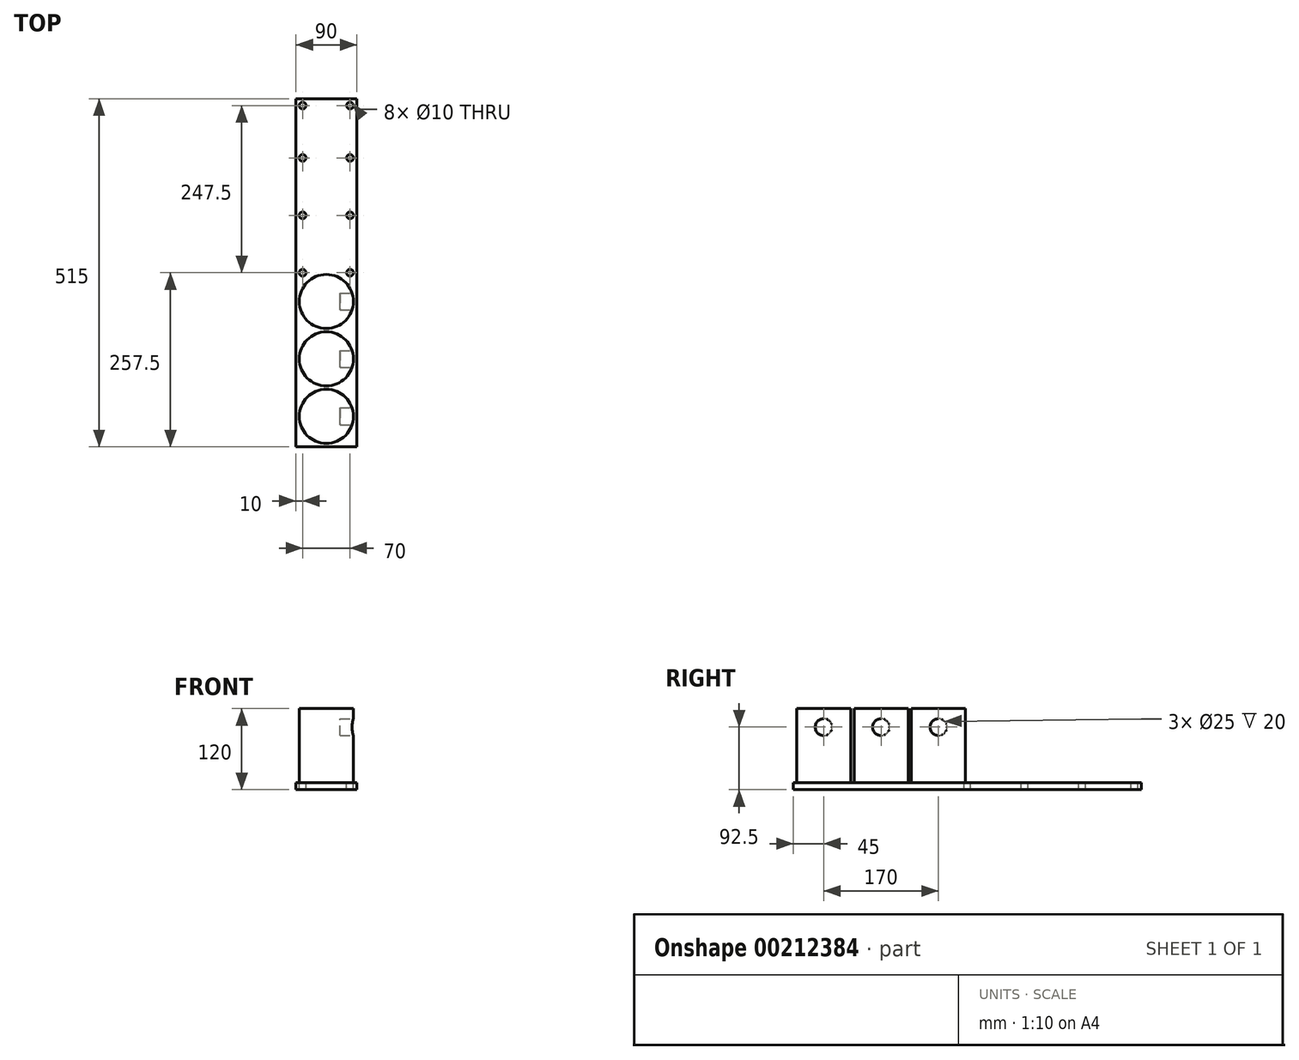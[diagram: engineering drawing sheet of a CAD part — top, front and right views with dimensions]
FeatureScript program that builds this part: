
annotation { "Feature Type Name" : "Feature", "Feature Type Description" : "" }
export const myFeature = defineFeature(function(context is Context, id is Id, definition is map)
    precondition{}
    {
        {
            var Q0;
            Q0=qCreatedBy(makeId("Right.planeOp"),FACE);
            var sketch = newSketch(context, id + "F0", { "sketchPlane" : qUnion([Q0])});
            skLineSegment(sketch, "E0.bottom", {"start": v(-257.5, 60) * mm, "end": v(257.5, 60) * mm});
            skLineSegment(sketch, "E0.top", {"start": v(-257.5, -60) * mm, "end": v(257.5, -60) * mm});
            skLineSegment(sketch, "E0.left", {"start": v(-257.5, 60) * mm, "end": v(-257.5, -60) * mm});
            skLineSegment(sketch, "E0.right", {"start": v(257.5, 60) * mm, "end": v(257.5, -60) * mm});
            skPoint(sketch, "E0.middle", {"position": v(0, 0) * mm});
            skSolve(sketch);
        }
        {
            var Q0;
            Q0=makeQuery(id+"F0.imprint","IMPRINT",FACE,{"disambiguationData":[TD([[makeQuery(id+"F0.imprint","IMPRINT",EDGE,{"derivedFrom":sQuery(id+"F0.wireOp",EDGE,"E0.bottom")}),-1.0]])]});
            extrude(context, id + "F1", {"entities" : qUnion([Q0]), "depth" : 90 * mm});
        }
        {
            var Q0;
            Q0=makeQuery(id+"F1.opExtrude","SWEPT_FACE",FACE,{"disambiguationData":[OSD([sQuery(id+"F0.wireOp",EDGE,"E0.bottom")])]});
            var sketch = newSketch(context, id + "F2", { "sketchPlane" : qUnion([Q0])});
            skCircle(sketch, "E1", {"center": v(45, 212.5) * mm, "radius": 40 * mm});
            skCircle(sketch, "E2", {"center": v(45, 127.5) * mm, "radius": 40 * mm});
            skCircle(sketch, "E3", {"center": v(45, 42.5) * mm, "radius": 40 * mm});
            skCircle(sketch, "E4.MirrorC", {"center": v(45, -42.5) * mm, "radius": 40 * mm});
            skCircle(sketch, "E5.MirrorC", {"center": v(45, -127.5) * mm, "radius": 40 * mm});
            skCircle(sketch, "E6.MirrorC", {"center": v(45, -212.5) * mm, "radius": 40 * mm});
            skSolve(sketch);
        }
        {
            var Q0;
            Q0=makeQuery(id+"F2.imprint","IMPRINT",FACE,{"disambiguationData":[TD([[makeQuery(id+"F2.imprint","IMPRINT",EDGE,{"derivedFrom":sQuery(id+"F2.wireOp",EDGE,"E1")}),1.0]])]});
            var Q1;
            Q1=makeQuery(id+"F2.imprint","IMPRINT",FACE,{"disambiguationData":[TD([[makeQuery(id+"F2.imprint","IMPRINT",EDGE,{"derivedFrom":sQuery(id+"F2.wireOp",EDGE,"E2")}),1.0]])]});
            var Q2;
            Q2=makeQuery(id+"F2.imprint","IMPRINT",FACE,{"disambiguationData":[TD([[makeQuery(id+"F2.imprint","IMPRINT",EDGE,{"derivedFrom":sQuery(id+"F2.wireOp",EDGE,"E3")}),1.0]])]});
            var Q3;
            Q3=makeQuery(id+"F2.imprint","IMPRINT",FACE,{"disambiguationData":[TD([[makeQuery(id+"F2.imprint","IMPRINT",EDGE,{"derivedFrom":sQuery(id+"F2.wireOp",EDGE,"E4.MirrorC")}),-1.0]])]});
            var Q4;
            Q4=makeQuery(id+"F2.imprint","IMPRINT",FACE,{"disambiguationData":[TD([[makeQuery(id+"F2.imprint","IMPRINT",EDGE,{"derivedFrom":sQuery(id+"F2.wireOp",EDGE,"E5.MirrorC")}),-1.0]])]});
            var Q5;
            Q5=makeQuery(id+"F2.imprint","IMPRINT",FACE,{"disambiguationData":[TD([[makeQuery(id+"F2.imprint","IMPRINT",EDGE,{"derivedFrom":sQuery(id+"F2.wireOp",EDGE,"E6.MirrorC")}),-1.0]])]});
            extrude(context, id + "F3", {"entities" : qUnion([Q0, Q1, Q2, Q3, Q4, Q5]), "operationType" : NewBodyOperationType.REMOVE, "oppositeDirection" : true, "depth" : 110 * mm});
        }
        {
            var Q0;
            Q0=makeQuery(id+"F1.opExtrude","CAP_FACE",FACE,{"disambiguationData":[OSD([sQuery(id+"F0.wireOp",EDGE,"E0.bottom"),sQuery(id+"F0.wireOp",EDGE,"E0.top"),sQuery(id+"F0.wireOp",EDGE,"E0.left"),sQuery(id+"F0.wireOp",EDGE,"E0.right")])],"isStart":false});
            var sketch = newSketch(context, id + "F4", { "sketchPlane" : qUnion([Q0])});
            skCircle(sketch, "E7", {"center": v(-212.5, 32.5) * mm, "radius": 12.5 * mm});
            skCircle(sketch, "E8", {"center": v(-42.5, 32.5) * mm, "radius": 12.5 * mm});
            skCircle(sketch, "E9", {"center": v(-127.5, 32.5) * mm, "radius": 12.5 * mm});
            skCircle(sketch, "E10.MirrorC", {"center": v(42.5, 32.5) * mm, "radius": 12.5 * mm});
            skCircle(sketch, "E11.MirrorC", {"center": v(127.5, 32.5) * mm, "radius": 12.5 * mm});
            skCircle(sketch, "E12.MirrorC", {"center": v(212.5, 32.5) * mm, "radius": 12.5 * mm});
            skSolve(sketch);
        }
        {
            var Q0;
            Q0=makeQuery(id+"F4.imprint","IMPRINT",FACE,{"disambiguationData":[TD([[makeQuery(id+"F4.imprint","IMPRINT",EDGE,{"derivedFrom":sQuery(id+"F4.wireOp",EDGE,"E9")}),1.0]])]});
            var Q1;
            Q1=makeQuery(id+"F4.imprint","IMPRINT",FACE,{"disambiguationData":[TD([[makeQuery(id+"F4.imprint","IMPRINT",EDGE,{"derivedFrom":sQuery(id+"F4.wireOp",EDGE,"E7")}),1.0]])]});
            var Q2;
            Q2=makeQuery(id+"F4.imprint","IMPRINT",FACE,{"disambiguationData":[TD([[makeQuery(id+"F4.imprint","IMPRINT",EDGE,{"derivedFrom":sQuery(id+"F4.wireOp",EDGE,"E8")}),1.0]])]});
            var Q3;
            Q3=makeQuery(id+"F4.imprint","IMPRINT",FACE,{"disambiguationData":[TD([[makeQuery(id+"F4.imprint","IMPRINT",EDGE,{"derivedFrom":sQuery(id+"F4.wireOp",EDGE,"E10.MirrorC")}),-1.0]])]});
            var Q4;
            Q4=makeQuery(id+"F4.imprint","IMPRINT",FACE,{"disambiguationData":[TD([[makeQuery(id+"F4.imprint","IMPRINT",EDGE,{"derivedFrom":sQuery(id+"F4.wireOp",EDGE,"E11.MirrorC")}),-1.0]])]});
            var Q5;
            Q5=makeQuery(id+"F4.imprint","IMPRINT",FACE,{"disambiguationData":[TD([[makeQuery(id+"F4.imprint","IMPRINT",EDGE,{"derivedFrom":sQuery(id+"F4.wireOp",EDGE,"E12.MirrorC")}),-1.0]])]});
            extrude(context, id + "F5", {"entities" : qUnion([Q0, Q1, Q2, Q3, Q4, Q5]), "operationType" : NewBodyOperationType.REMOVE, "oppositeDirection" : true, "depth" : 25 * mm});
        }
        {
            var Q0;
            Q0=makeQuery(id+"F1.opExtrude","SWEPT_FACE",FACE,{"disambiguationData":[OSD([sQuery(id+"F0.wireOp",EDGE,"E0.bottom")])]});
            var sketch = newSketch(context, id + "F6", { "sketchPlane" : qUnion([Q0])});
            skCircle(sketch, "E13", {"center": v(10, 247.5) * mm, "radius": 5 * mm});
            skCircle(sketch, "E14", {"center": v(80, 247.5) * mm, "radius": 5 * mm});
            skCircle(sketch, "E15", {"center": v(10, 170) * mm, "radius": 5 * mm});
            skCircle(sketch, "E16", {"center": v(80, 170) * mm, "radius": 5 * mm});
            skCircle(sketch, "E17", {"center": v(10, 85) * mm, "radius": 5 * mm});
            skCircle(sketch, "E18", {"center": v(80, 85) * mm, "radius": 5 * mm});
            skCircle(sketch, "E19.MirrorC", {"center": v(10, -85) * mm, "radius": 5 * mm});
            skCircle(sketch, "E20.MirrorC", {"center": v(80, -85) * mm, "radius": 5 * mm});
            skCircle(sketch, "E21.MirrorC", {"center": v(80, -170) * mm, "radius": 5 * mm});
            skCircle(sketch, "E22.MirrorC", {"center": v(10, -170) * mm, "radius": 5 * mm});
            skCircle(sketch, "E23.MirrorC", {"center": v(10, -247.5) * mm, "radius": 5 * mm});
            skCircle(sketch, "E24.MirrorC", {"center": v(80, -247.5) * mm, "radius": 5 * mm});
            skCircle(sketch, "E25", {"center": v(80, 0) * mm, "radius": 5 * mm});
            skCircle(sketch, "E26", {"center": v(10, 0) * mm, "radius": 5 * mm});
            skSolve(sketch);
        }
        {
            var Q0;
            Q0=makeQuery(id+"F6.imprint","IMPRINT",FACE,{"disambiguationData":[TD([[makeQuery(id+"F6.imprint","IMPRINT",EDGE,{"derivedFrom":sQuery(id+"F6.wireOp",EDGE,"E16")}),1.0]])]});
            var Q1;
            Q1=makeQuery(id+"F6.imprint","IMPRINT",FACE,{"disambiguationData":[TD([[makeQuery(id+"F6.imprint","IMPRINT",EDGE,{"derivedFrom":sQuery(id+"F6.wireOp",EDGE,"E14")}),1.0]])]});
            var Q2;
            Q2=makeQuery(id+"F6.imprint","IMPRINT",FACE,{"disambiguationData":[TD([[makeQuery(id+"F6.imprint","IMPRINT",EDGE,{"derivedFrom":sQuery(id+"F6.wireOp",EDGE,"E18")}),1.0]])]});
            var Q3;
            Q3=makeQuery(id+"F6.imprint","IMPRINT",FACE,{"disambiguationData":[TD([[makeQuery(id+"F6.imprint","IMPRINT",EDGE,{"derivedFrom":sQuery(id+"F6.wireOp",EDGE,"E17")}),1.0]])]});
            var Q4;
            Q4=makeQuery(id+"F6.imprint","IMPRINT",FACE,{"disambiguationData":[TD([[makeQuery(id+"F6.imprint","IMPRINT",EDGE,{"derivedFrom":sQuery(id+"F6.wireOp",EDGE,"E15")}),1.0]])]});
            var Q5;
            Q5=makeQuery(id+"F6.imprint","IMPRINT",FACE,{"disambiguationData":[TD([[makeQuery(id+"F6.imprint","IMPRINT",EDGE,{"derivedFrom":sQuery(id+"F6.wireOp",EDGE,"E13")}),1.0]])]});
            var Q6;
            Q6=makeQuery(id+"F6.imprint","IMPRINT",FACE,{"disambiguationData":[TD([[makeQuery(id+"F6.imprint","IMPRINT",EDGE,{"derivedFrom":sQuery(id+"F6.wireOp",EDGE,"SPK6fGLj-2rl5-jWPP-p8Vn-sWfGEhAaPwNL")}),1.0]])]});
            var Q7;
            Q7=makeQuery(id+"F6.imprint","IMPRINT",FACE,{"disambiguationData":[TD([[makeQuery(id+"F6.imprint","IMPRINT",EDGE,{"derivedFrom":sQuery(id+"F6.wireOp",EDGE,"E25")}),1.0]])]});
            var Q8;
            Q8=makeQuery(id+"F6.imprint","IMPRINT",FACE,{"disambiguationData":[TD([[makeQuery(id+"F6.imprint","IMPRINT",EDGE,{"derivedFrom":sQuery(id+"F6.wireOp",EDGE,"E20.MirrorC")}),-1.0]])]});
            var Q9;
            Q9=makeQuery(id+"F6.imprint","IMPRINT",FACE,{"disambiguationData":[TD([[makeQuery(id+"F6.imprint","IMPRINT",EDGE,{"derivedFrom":sQuery(id+"F6.wireOp",EDGE,"E19.MirrorC")}),-1.0]])]});
            var Q10;
            Q10=makeQuery(id+"F6.imprint","IMPRINT",FACE,{"disambiguationData":[TD([[makeQuery(id+"F6.imprint","IMPRINT",EDGE,{"derivedFrom":sQuery(id+"F6.wireOp",EDGE,"E22.MirrorC")}),-1.0]])]});
            var Q11;
            Q11=makeQuery(id+"F6.imprint","IMPRINT",FACE,{"disambiguationData":[TD([[makeQuery(id+"F6.imprint","IMPRINT",EDGE,{"derivedFrom":sQuery(id+"F6.wireOp",EDGE,"E21.MirrorC")}),-1.0]])]});
            var Q12;
            Q12=makeQuery(id+"F6.imprint","IMPRINT",FACE,{"disambiguationData":[TD([[makeQuery(id+"F6.imprint","IMPRINT",EDGE,{"derivedFrom":sQuery(id+"F6.wireOp",EDGE,"E24.MirrorC")}),-1.0]])]});
            var Q13;
            Q13=makeQuery(id+"F6.imprint","IMPRINT",FACE,{"disambiguationData":[TD([[makeQuery(id+"F6.imprint","IMPRINT",EDGE,{"derivedFrom":sQuery(id+"F6.wireOp",EDGE,"E23.MirrorC")}),-1.0]])]});
            var Q14;
            Q14=sQuery(id+"F6.wireOp",EDGE,"E24.MirrorC");
            var Q15;
            Q15=sQuery(id+"F6.wireOp",EDGE,"E23.MirrorC");
            var Q16;
            Q16=sQuery(id+"F6.wireOp",EDGE,"E22.MirrorC");
            var Q17;
            Q17=sQuery(id+"F6.wireOp",EDGE,"E21.MirrorC");
            var Q18;
            Q18=sQuery(id+"F6.wireOp",EDGE,"E20.MirrorC");
            var Q19;
            Q19=sQuery(id+"F6.wireOp",EDGE,"E19.MirrorC");
            var Q20;
            Q20=sQuery(id+"F6.wireOp",EDGE,"SPK6fGLj-2rl5-jWPP-p8Vn-sWfGEhAaPwNL");
            var Q21;
            Q21=sQuery(id+"F6.wireOp",EDGE,"E25");
            var Q22;
            Q22=sQuery(id+"F6.wireOp",EDGE,"E18");
            var Q23;
            Q23=sQuery(id+"F6.wireOp",EDGE,"E17");
            var Q24;
            Q24=sQuery(id+"F6.wireOp",EDGE,"E16");
            var Q25;
            Q25=sQuery(id+"F6.wireOp",EDGE,"E15");
            var Q26;
            Q26=sQuery(id+"F6.wireOp",EDGE,"E13");
            var Q27;
            Q27=sQuery(id+"F6.wireOp",EDGE,"E14");
            extrude(context, id + "F7", {"entities" : qUnion([Q0, Q1, Q2, Q3, Q4, Q5, Q6, Q7, Q8, Q9, Q10, Q11, Q12, Q13]), "operationType" : NewBodyOperationType.REMOVE, "surfaceEntities" : qUnion([Q14, Q15, Q16, Q17, Q18, Q19, Q20, Q21, Q22, Q23, Q24, Q25, Q26, Q27]), "oppositeDirection" : true, "depth" : 120 * mm});
        }
        {
            var Q0;
            Q0=makeQuery(id+"F6.imprint","IMPRINT",FACE,{"disambiguationData":[TD([[makeQuery(id+"F6.imprint","IMPRINT",EDGE,{"derivedFrom":sQuery(id+"F6.wireOp",EDGE,"E26")}),1.0]])]});
            extrude(context, id + "F8", {"entities" : qUnion([Q0]), "operationType" : NewBodyOperationType.REMOVE, "oppositeDirection" : true, "depth" : 120 * mm});
        }
    });
